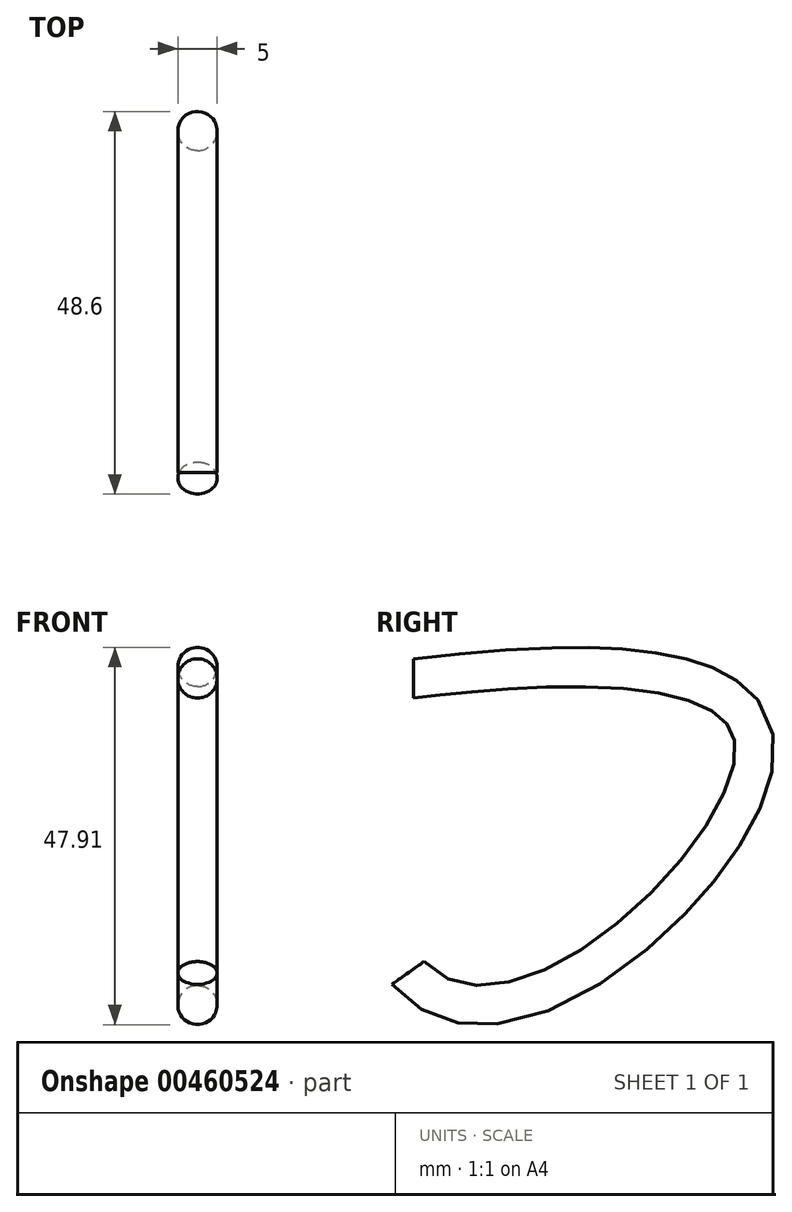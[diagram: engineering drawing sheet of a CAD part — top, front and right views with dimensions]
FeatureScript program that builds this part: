
annotation { "Feature Type Name" : "Feature", "Feature Type Description" : "" }
export const myFeature = defineFeature(function(context is Context, id is Id, definition is map)
    precondition{}
    {
        {
            var Q0;
            Q0=qCreatedBy(makeId("Front.planeOp"),FACE);
            var sketch = newSketch(context, id + "F0", { "sketchPlane" : qUnion([Q0])});
            skCircle(sketch, "E0", {"center": v(0, 7.78) * mm, "radius": 2.5 * mm});
            skSolve(sketch);
        }
        {
            var Q0;
            Q0=qCreatedBy(makeId("Right.planeOp"),FACE);
            var sketch = newSketch(context, id + "F1", { "sketchPlane" : qUnion([Q0])});
            skFitSpline(sketch, "E1", {"points": [v(0, 6.93) * mm, v(42.42, 0) * mm, v(0, -29.14) * mm], "startDerivative": vector(67.46, 7.72) * mm, "endDerivative": vector(-73.92, 82.2) * mm});
            skSolve(sketch);
        }
        {
            var Q0;
            Q0 = qSketchRegion(id + "F0", true);
            var Q1;
            Q1 = qConstructionFilter(qBodyType(qCreatedBy(id + "F1" ,EDGE), BodyType.WIRE), ConstructionObject.NO);
            sweep(context, id + "F2", {"profiles" : qUnion([Q0]), "path" : qUnion([Q1])});
        }
    });
